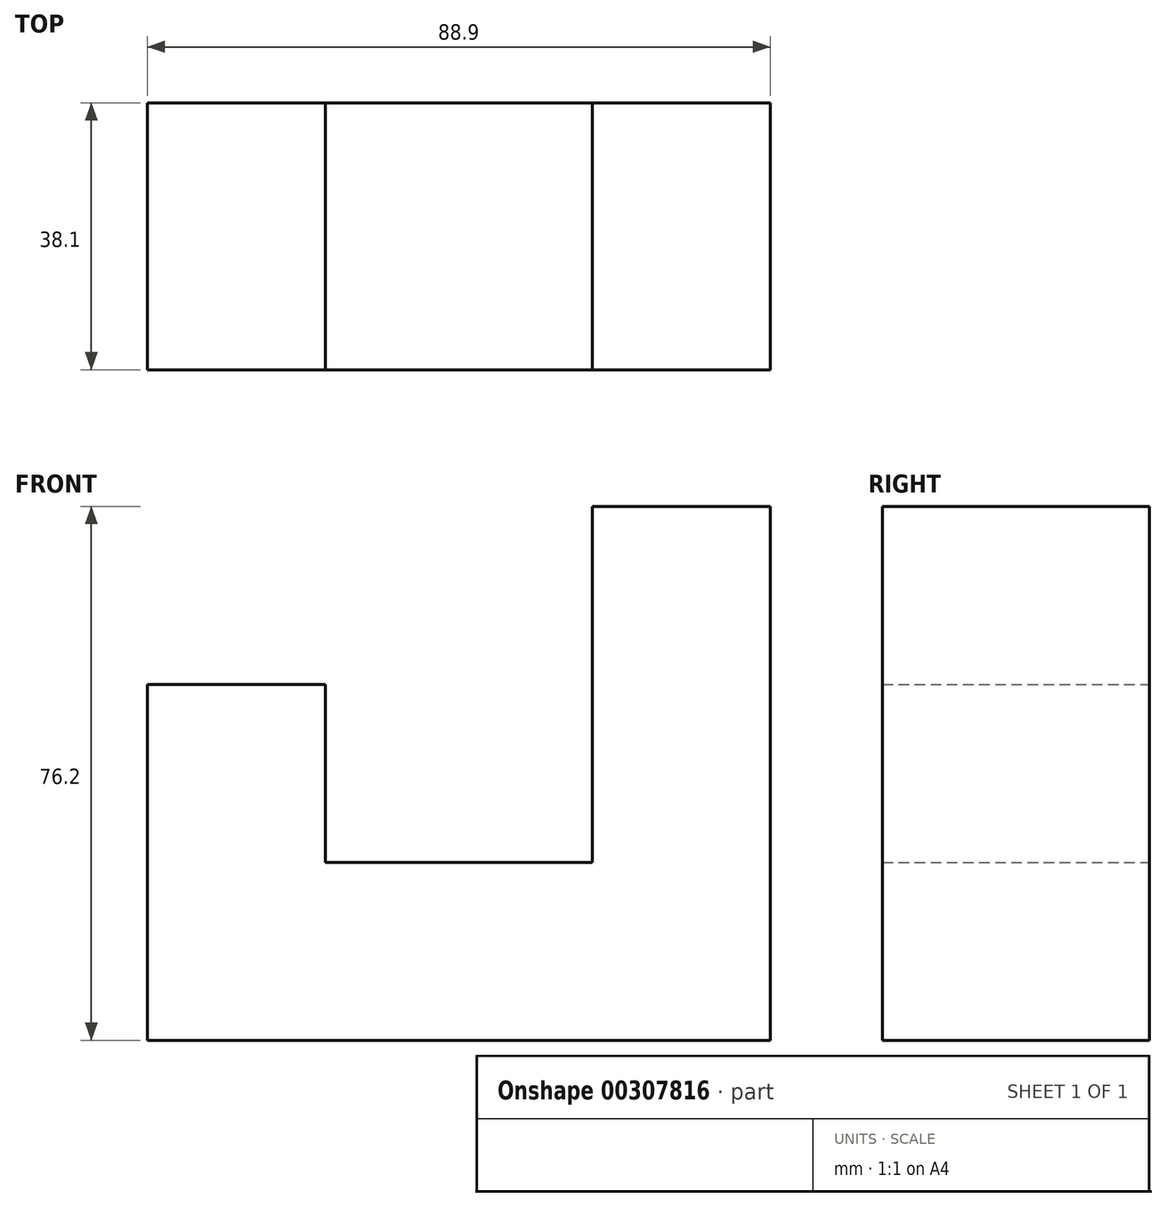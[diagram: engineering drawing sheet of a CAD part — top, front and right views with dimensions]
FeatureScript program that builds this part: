
annotation { "Feature Type Name" : "Feature", "Feature Type Description" : "" }
export const myFeature = defineFeature(function(context is Context, id is Id, definition is map)
    precondition{}
    {
        {
            var Q0;
            Q0=qCreatedBy(makeId("Front.planeOp"),FACE);
            var sketch = newSketch(context, id + "F0", { "sketchPlane" : qUnion([Q0])});
            skLineSegment(sketch, "E0", {"start": v(-38.46, -51.54) * mm, "end": v(50.44, -51.54) * mm});
            skLineSegment(sketch, "E1", {"start": v(-38.46, -51.54) * mm, "end": v(-38.46, -26.14) * mm});
            skLineSegment(sketch, "E2", {"start": v(4.32, -26.14) * mm, "end": v(25.04, -26.14) * mm});
            skLineSegment(sketch, "E3", {"start": v(25.04, -26.14) * mm, "end": v(25.04, 24.66) * mm});
            skLineSegment(sketch, "E4", {"start": v(25.04, 24.66) * mm, "end": v(50.44, 24.66) * mm});
            skLineSegment(sketch, "E5", {"start": v(50.44, 24.66) * mm, "end": v(50.44, -51.54) * mm});
            skLineSegment(sketch, "E6", {"start": v(-38.46, -26.14) * mm, "end": v(-38.46, -0.74) * mm});
            skLineSegment(sketch, "E7", {"start": v(-38.46, -0.74) * mm, "end": v(-13.06, -0.74) * mm});
            skLineSegment(sketch, "E8", {"start": v(-13.06, -0.74) * mm, "end": v(-13.06, -26.14) * mm});
            skLineSegment(sketch, "E9", {"start": v(-13.06, -26.14) * mm, "end": v(25.04, -26.14) * mm});
            skSolve(sketch);
        }
        {
            var Q0;
            Q0=makeQuery(id+"F0.imprint","IMPRINT",FACE,{"disambiguationData":[TD([[makeQuery(id+"F0.imprint","IMPRINT",EDGE,{"derivedFrom":sQuery(id+"F0.wireOp",EDGE,"E0")}),1.0]])]});
            extrude(context, id + "F1", {"entities" : qUnion([Q0]), "depth" : 38.1 * mm});
        }
    });
